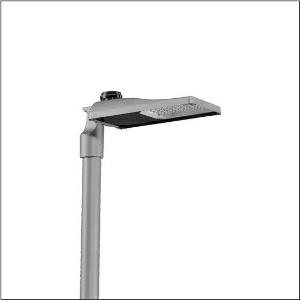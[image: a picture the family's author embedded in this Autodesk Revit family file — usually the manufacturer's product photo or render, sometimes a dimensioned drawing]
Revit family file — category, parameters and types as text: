
# Revit family: streetlight_sl_31_mini___st1_0a_5xh6d3bn08ja_1c18
name_source: partatom
category: Lighting Fixtures
units: mm (PartAtom-declared; Revit-internal decimal feet)

## family parameters
Cut with Voids When Loaded = No
Host = Face
Light Source = No
Part Type = Normal
Room Calculation Point = No
Round Connector Dimension = Use Diameter
Shared = No

## types (1)
- --- (1 x LED, 12140 lm, 81.1 W, 3000K)
    Apparent Load = 81 VA
    CIE Flux Codes = 40 73 97 100 100
    Color Rendering = 70
    Color Temperature = 3000K
    Default Elevation = 1800 mm
    Description = Streetlight SL 31 mini NEMA (7pin) mast luminaire for post-top, side-entry; light control with lens of PMMA; light distribution: ST1.0a, direct asymmetric distribution, for standard-compliant lighting for roads and squares; LED: luminous flux: 12.140lm, light colour: 730, colour temperature: 3000K; luminous efficacy: 149,7lm/W; control: pre-setting: linear dimming characteristic, flexible luminous flux parameterisation, time-dependent luminous flux control, constant luminous flux control, intelligent temperature release in ECG and LED module, overheat protection; luminaire housing, of diecast aluminium, SITECO metallic grey (DB 702S), corrosivity category C5 high according to DIN EN ISO 12944; cover of toughened safety glass, transparent, opened without tools; mast flange of diecast aluminium, SITECO metallic grey (DB 702S), spigot size: 76/60mm, mast flange included unmounted; cable length: 10,5m, connection cable pre-assembled; mains connection: 220..240V, AC, 50/60Hz; power consumption (at start of service life): 81,1W / (at end of service life): 88,3W / (with reduced operation 50%): 36,4W; protection rating (complete): IP66; insulation class (complete): insulation class I (protective earthing); impact resistance: IK10; certification: CE, ENEC, ENEC+, VDE, UKCA; permissible operating ambient temperature for outdoor applications: -40..+50°C; packaging unit: 1 piece

Light Distribution: ST1.0a
    Height = 76 mm
    Lamp = 1 x LED
    Lamp Light Flux = 12140 lm
    Lamp Power = 81.1 W
    Lamp count = 1
    Length = 547 mm
    Luminous efficacy = 150 lm/W
    Manufacturer = Siteco
    ModVariant = No
    Model = 5XH6D3BN08JA
    Number of Poles = 1
    OnlyDefault = Yes
    Power Factor = 1
    Product Name = Streetlight SL 31 mini | ST1.0a
    Product group = mast luminaire | pylon top
    ProductGroupID = 6100
    Protection Class = Protection class I
    Protection Degree = IP 66
    RLX_Detail_Level = 1
    RLX_Emergency_Light_Flux = 0 lm
    RLX_Emergency_Type = 0
    RLX_Emergency_Type_DB = No
    RlxData = <blob elided: 40253 chars, md5=5759d0ea>
    Socket = socket
    Standby Power = 0 W
    System Light Flux = 12140 lm
    System Power = 81 W
    Type Comments = factory setting: luminous flux: 100 % | dim-lin: 254 | 860 mA
    Type Image = l_1300322.jpg
    URL = http://relux.com
    VarID = @adj_056955
    Voltage = 0 V
    Weight = 0.00 kg
    Width = 265 mm

## geometry (parser evidence)
native form markers: Blend x4, Sweep x11
no freeform markers — native parametric forms only
